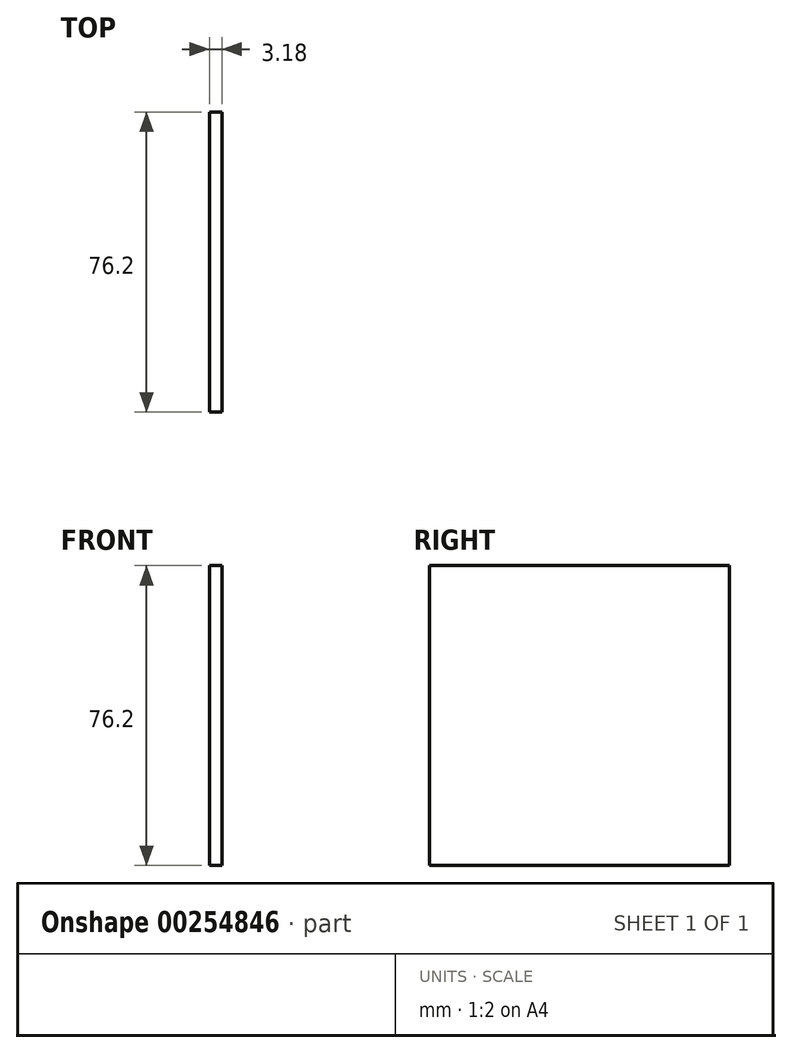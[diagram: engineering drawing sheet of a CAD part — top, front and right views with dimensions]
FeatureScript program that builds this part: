
annotation { "Feature Type Name" : "Feature", "Feature Type Description" : "" }
export const myFeature = defineFeature(function(context is Context, id is Id, definition is map)
    precondition{}
    {
        {
            var Q0;
            Q0=qCreatedBy(makeId("Right.planeOp"),FACE);
            var sketch = newSketch(context, id + "F0", { "sketchPlane" : qUnion([Q0])});
            skLineSegment(sketch, "E0.bottom", {"start": v(-38.1, -38.1) * mm, "end": v(38.1, -38.1) * mm});
            skLineSegment(sketch, "E0.top", {"start": v(-38.1, 38.1) * mm, "end": v(38.1, 38.1) * mm});
            skLineSegment(sketch, "E0.left", {"start": v(-38.1, -38.1) * mm, "end": v(-38.1, 38.1) * mm});
            skLineSegment(sketch, "E0.right", {"start": v(38.1, -38.1) * mm, "end": v(38.1, 38.1) * mm});
            skPoint(sketch, "E0.middle", {"position": v(0, 0) * mm});
            skSolve(sketch);
        }
        {
            var Q0;
            Q0=makeQuery(id+"F0.imprint","IMPRINT",FACE,{"disambiguationData":[TD([[makeQuery(id+"F0.imprint","IMPRINT",EDGE,{"derivedFrom":sQuery(id+"F0.wireOp",EDGE,"E0.bottom")}),1.0]])]});
            extrude(context, id + "F1", {"entities" : qUnion([Q0]), "endBound" : BoundingType.SYMMETRIC, "depth" : 3.17 * mm});
        }
    });
